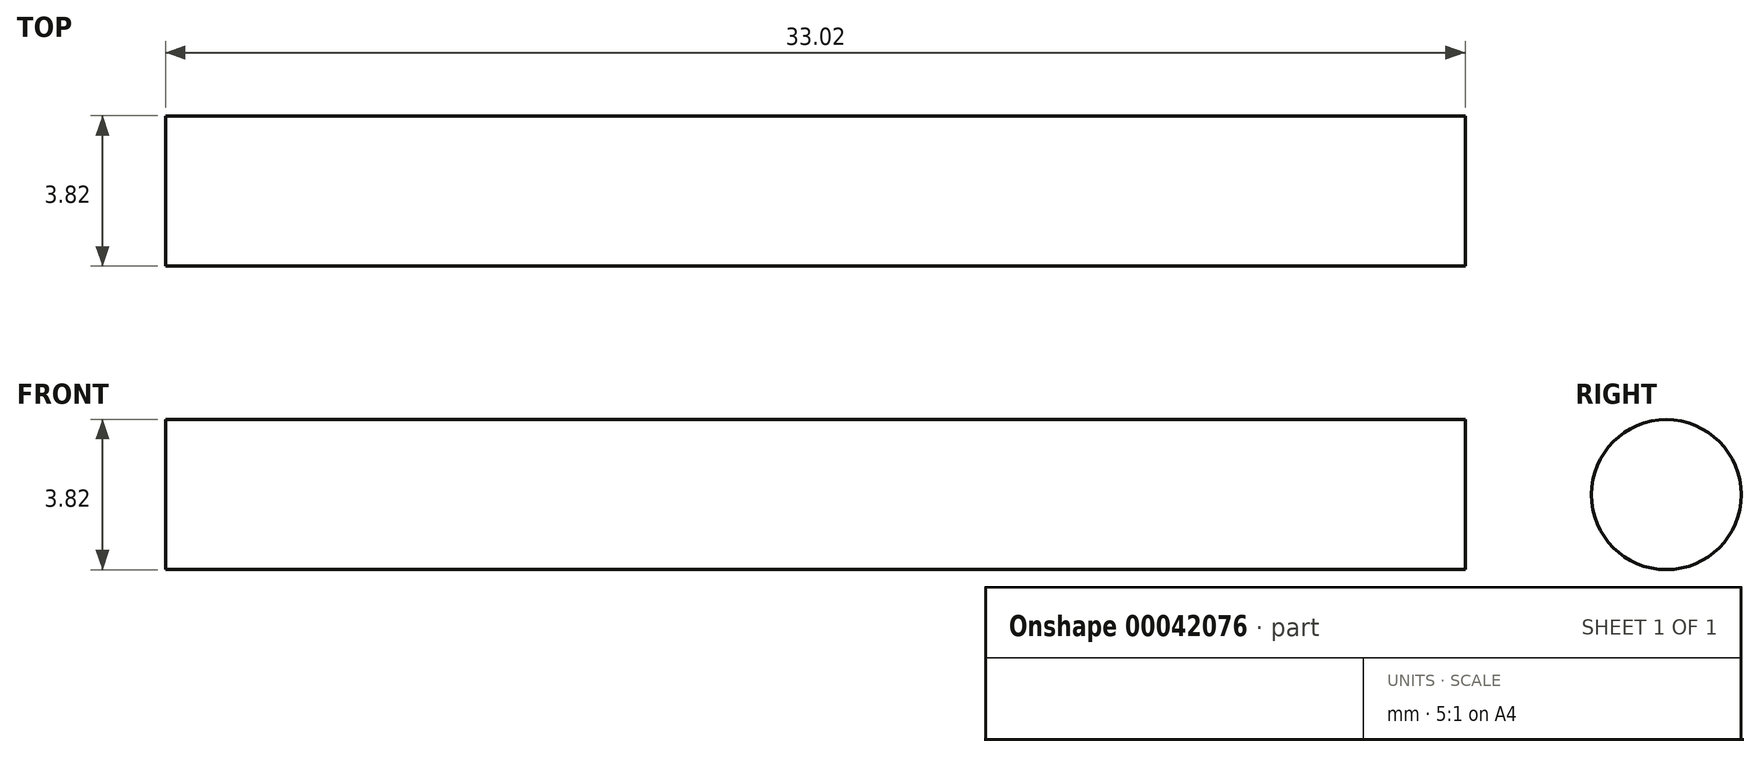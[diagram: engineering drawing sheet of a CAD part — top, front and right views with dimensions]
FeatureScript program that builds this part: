
annotation { "Feature Type Name" : "Feature", "Feature Type Description" : "" }
export const myFeature = defineFeature(function(context is Context, id is Id, definition is map)
    precondition{}
    {
        {
            var Q0;
            Q0=qCreatedBy(makeId("Right.planeOp"),FACE);
            var sketch = newSketch(context, id + "F0", { "sketchPlane" : qUnion([Q0])});
            skCircle(sketch, "E0", {"center": v(0, 0) * mm, "radius": 1.9 * mm});
            skSolve(sketch);
        }
        {
            var Q0;
            Q0 = qSketchRegion(id + "F0", true);
            extrude(context, id + "F1", {"entities" : qUnion([Q0]), "endBound" : BoundingType.SYMMETRIC, "depth" : 33.02 * mm});
        }
    });
